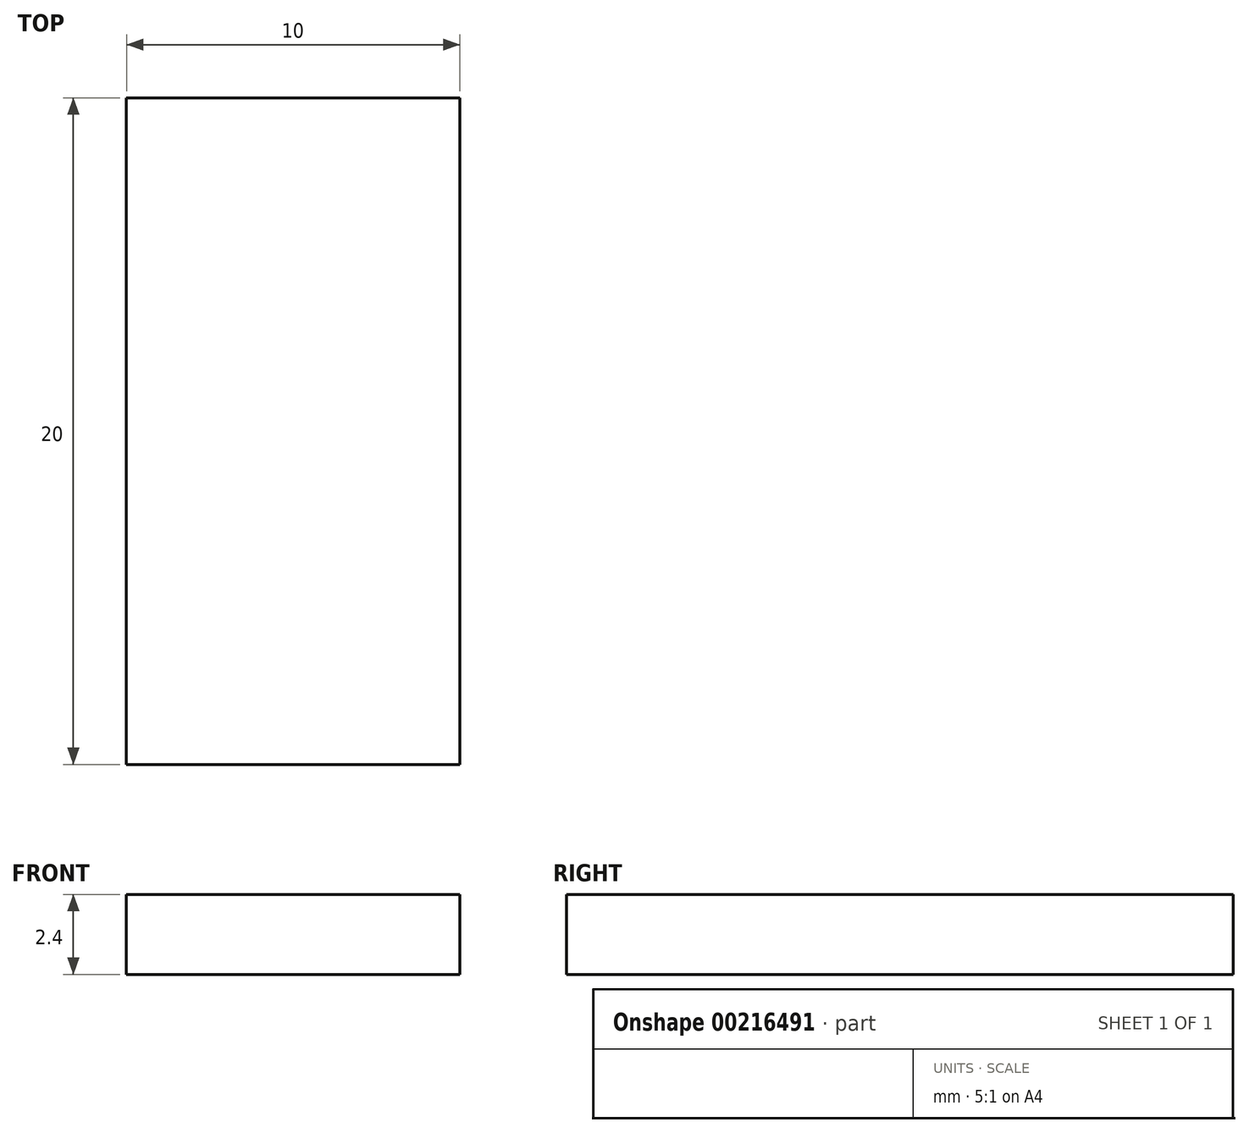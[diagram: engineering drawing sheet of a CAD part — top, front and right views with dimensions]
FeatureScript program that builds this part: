
annotation { "Feature Type Name" : "Feature", "Feature Type Description" : "" }
export const myFeature = defineFeature(function(context is Context, id is Id, definition is map)
    precondition{}
    {
        {
            var Q0;
            Q0=qCreatedBy(makeId("Top.planeOp"),FACE);
            var sketch = newSketch(context, id + "F0", { "sketchPlane" : qUnion([Q0])});
            skLineSegment(sketch, "E0.bottom", {"start": v(8.47, 10) * mm, "end": v(-1.53, 10) * mm});
            skLineSegment(sketch, "E0.top", {"start": v(8.47, -10) * mm, "end": v(-1.53, -10) * mm});
            skLineSegment(sketch, "E0.left", {"start": v(8.47, 10) * mm, "end": v(8.47, -10) * mm});
            skLineSegment(sketch, "E0.right", {"start": v(-1.53, 10) * mm, "end": v(-1.53, -10) * mm});
            skPoint(sketch, "E0.middle", {"position": v(3.47, 0) * mm});
            skSolve(sketch);
        }
        {
            var Q0;
            Q0 = qSketchRegion(id + "F0", true);
            extrude(context, id + "F1", {"entities" : qUnion([Q0]), "depth" : 2.4 * mm, "offsetDistance" : 25 * mm});
        }
    });
